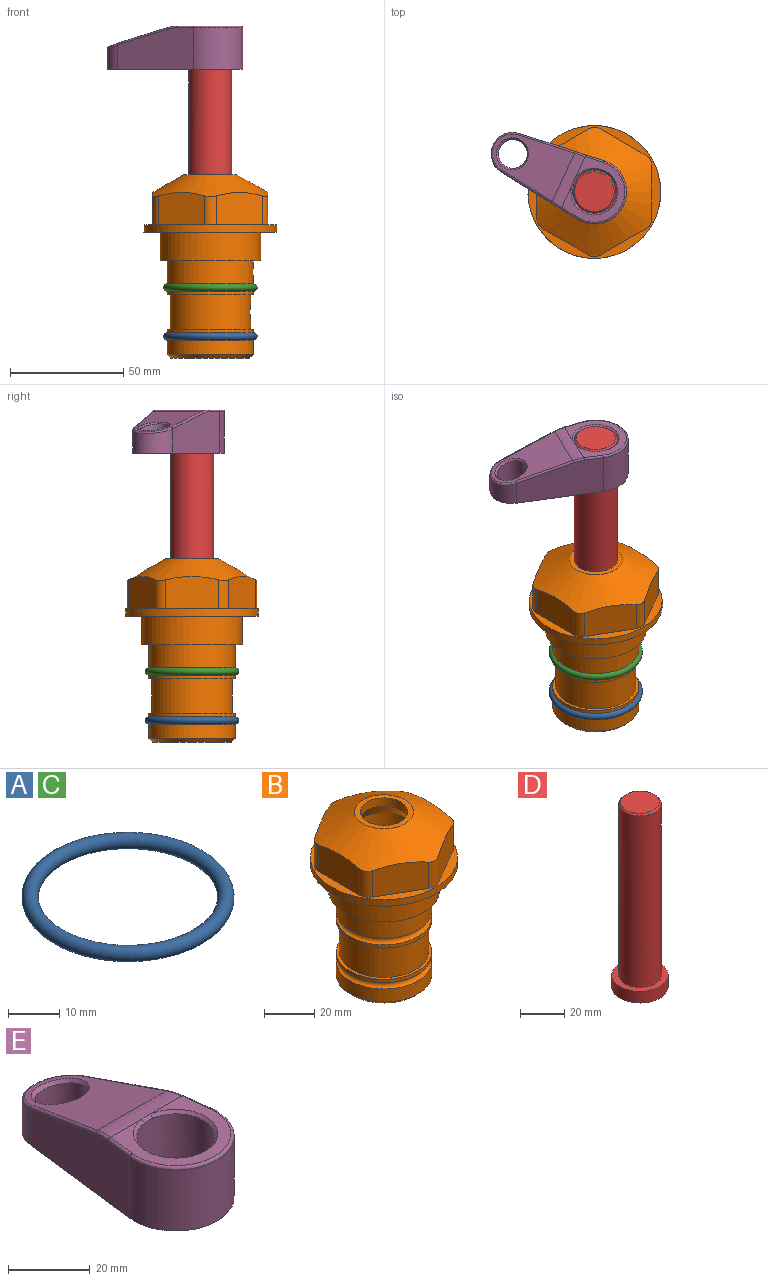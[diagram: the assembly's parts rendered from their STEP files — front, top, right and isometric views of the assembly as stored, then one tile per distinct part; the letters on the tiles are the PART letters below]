
ASSEMBLY  parts=5 mates=4
PART A: 1 faces, bbox 44.7x44.7x3.2 mm
  f0: torus R=19.05mm, axis (0,0,1), area 1193.9mm2
PART B: 36 faces, bbox 58.7x58.7x81 mm
  f0: cylinder r=17.78mm len=35.56mm, axis (0,0,1), area 1670.8mm2, adj f23,f24,f31
  f1: cylinder r=19.05mm len=38.1mm, axis (0,0,1), area 1191.9mm2, adj f26,f27,f30
  f2: plane 58.66x58.66mm, normal (0,0,-1), area 1150.6mm2, adj f3,f28
  f3: cylinder r=29.33mm len=58.66mm, axis (0,0,-1), area 585.1mm2, adj f2,f4
  f4: plane 58.66x58.66mm, normal (0,0,1), area 475.9mm2, adj f3,f5,f6,f7,f8,f9,f10,f11
  f5: plane 20.32x14.34mm, normal (-0.5,0.87,0), area 324.4mm2, adj f4,f15,f16,f17
  f6: plane 20.32x14.34mm, normal (0.5,0.87,0), area 324.4mm2, adj f4,f14,f15,f17
  f7: plane 23.48x14.34mm, normal (1,0,0), area 324.4mm2, adj f4,f13,f14,f17
  f8: plane 20.32x14.34mm, normal (0.5,-0.87,0), area 324.4mm2, adj f4,f12,f13,f17
  f9: plane 20.32x14.34mm, normal (-0.5,-0.87,0), area 324.4mm2, adj f4,f11,f12,f17
  f10: plane 23.48x14.34mm, normal (-1,0,0), area 324.4mm2, adj f4,f11,f16,f17
  f11: cylinder r=5.08mm len=12.85mm, axis (0,0,-1), area 67.2mm2, adj f4,f9,f10,f17
  f12: cylinder r=5.08mm len=12.85mm, axis (0,0,-1), area 67.2mm2, adj f4,f8,f9,f17
  f13: cylinder r=5.08mm len=12.85mm, axis (0,0,-1), area 67.2mm2, adj f4,f7,f8,f17
  f14: cylinder r=5.08mm len=12.85mm, axis (0,0,-1), area 67.2mm2, adj f4,f6,f7,f17
  f15: cylinder r=5.08mm len=12.85mm, axis (0,0,-1), area 67.2mm2, adj f4,f5,f6,f17
  f16: cylinder r=5.08mm len=12.85mm, axis (0,0,-1), area 67.2mm2, adj f4,f5,f10,f17
  f17: cone r=11.73mm half-angle=60deg, axis (0,0,-1), area 2071.8mm2, adj f5,f6,f7,f8,f9,f10,f11,f12
  f18: plane 23.46x23.46mm, normal (0,0,1), area 147.4mm2, adj f17,f35
  f19: plane 34.93x34.93mm, normal (0,0,-1), area 958mm2, adj f29
  f20: cylinder r=19.05mm len=38.1mm, axis (0,0,1), area 760.1mm2, adj f21,f29
  f21: torus R=19.05mm, axis (0,0,1), area 565.3mm2, adj f20,f22
  f22: cylinder r=19.05mm len=38.1mm, axis (0,0,1), area 190mm2, adj f21,f23
  f23: plane 38.1x38.1mm, normal (0,0,1), area 146.9mm2, adj f0,f22
  f24: plane 38.1x38.1mm, normal (0,0,-1), area 146.9mm2, adj f0,f25
  f25: cylinder r=19.05mm len=38.1mm, axis (0,0,1), area 190mm2, adj f24,f26
  f26: torus R=19.05mm, axis (0,0,1), area 565.3mm2, adj f1,f25
  f27: plane 44.45x44.45mm, normal (0,0,-1), area 411.7mm2, adj f1,f28
  f28: cylinder r=22.23mm len=44.45mm, axis (0,0,1), area 1773.5mm2, adj f2,f27
  f29: cone r=19.05mm half-angle=45deg, axis (0,0,1), area 257.5mm2, adj f19,f20
  f30: cylinder r=3.17mm len=6.75mm, axis (-1,0,0), area 128mm2, adj f1,f33
  f31: cylinder r=3.17mm len=6.35mm, axis (-1,0,0), area 102.5mm2, adj f0,f33
  f32: plane 25.4x25.4mm, normal (0,0,1), area 506.7mm2, adj f33
  f33: cylinder r=12.7mm len=66.42mm, axis (0,0,-1), area 5236.2mm2, adj f30,f31,f32,f34
  f34: cone r=9.53mm half-angle=30deg, axis (0,0,-1), area 443.4mm2, adj f33,f35
  f35: cylinder r=9.53mm len=19.05mm, axis (0,0,-1), area 240.9mm2, adj f18,f34
PART C: same geometry as A
PART D: 6 faces, bbox 25.4x25.4x101.6 mm
  f0: plane 17.46x17.46mm, normal (0,0,1), area 239.5mm2, adj f5
  f1: plane 25.4x25.4mm, normal (0,0,-1), area 506.7mm2, adj f2
  f2: cylinder r=12.7mm len=25.4mm, axis (0,0,1), area 506.7mm2, adj f1,f3
  f3: plane 25.4x25.4mm, normal (0,0,1), area 221.7mm2, adj f2,f4
  f4: cylinder r=9.53mm len=94.46mm, axis (0,0,1), area 5653mm2, adj f3,f5
  f5: cone r=8.73mm half-angle=45deg, axis (0,0,-1), area 64.4mm2, adj f0,f4
PART E: 31 faces, bbox 31.7x65.5x19.8 mm
  f0: plane 39.12x18.26mm, normal (0.99,0.12,0), area 612.2mm2, adj f1,f4,f7,f11,f13,f15
  f1: cylinder r=9.53mm len=18.91mm, axis (0,0,-1), area 296.1mm2, adj f0,f2,f7,f17
  f2: plane 39.12x18.26mm, normal (-0.99,0.12,0), area 612.2mm2, adj f1,f4,f7,f12,f14,f16
  f3: cylinder r=6.35mm len=12.7mm, axis (0,0,-1), area 362.4mm2, adj f7,f18
  f4: cylinder r=14.29mm len=28.58mm, axis (0,0,-1), area 882.2mm2, adj f0,f2,f7,f10
  f5: cylinder r=9.53mm len=19.05mm, axis (0,0,-1), area 1092.6mm2, adj f7,f19,f20
  f6: plane 26.99x23.69mm, normal (0,0,1), area 216.2mm2, adj f9,f10,f11,f12,f19
  f7: plane 63.5x28.58mm, normal (0,0,-1), area 661.8mm2, adj f0,f1,f2,f3,f4,f5,f22,f23
  f8: plane 33.52x23.6mm, normal (0,0.26,0.97), area 486mm2, adj f9,f15,f16,f17,f18
  f9: cylinder r=19.05mm len=24.72mm, axis (1,0,0), area 120.4mm2, adj f6,f8,f13,f14,f20
  f10: torus R=13.49mm, axis (0,0,1), area 59mm2, adj f4,f6,f11,f12
  f11: cylinder r=0.79mm len=8.67mm, axis (0.12,-0.99,0), area 10.8mm2, adj f0,f6,f10,f13
  f12: cylinder r=0.79mm len=8.67mm, axis (0.12,0.99,0), area 10.8mm2, adj f2,f6,f10,f14
  f13: bspline ~4.95x1.42mm, area 6.1mm2, adj f0,f9,f11,f15
  f14: bspline ~4.95x1.42mm, area 6.1mm2, adj f2,f9,f12,f16
  f15: cylinder r=0.79mm len=25.95mm, axis (0.12,-0.96,0.26), area 32.9mm2, adj f0,f8,f13,f17
  f16: cylinder r=0.79mm len=25.95mm, axis (0.12,0.96,-0.26), area 32.9mm2, adj f2,f8,f14,f17
  f17: bspline ~18.91x8.38mm, area 30mm2, adj f1,f8,f15,f16
  f18: bspline ~14.29x14.29mm, area 48.3mm2, adj f3,f8
  f19: cone r=9.53mm half-angle=45deg, axis (0,0,1), area 66.5mm2, adj f5,f6,f20
  f20: bspline ~3.22x0.96mm, area 3.5mm2, adj f5,f9,f19
  f21: plane 2.75x2.72mm, normal (0,0,-1), area 2.9mm2, adj f23,f25,f28
  f22: plane 23.05x15.88mm, normal (-0.99,-0.12,0), area 323.6mm2, adj f7,f25,f26,f27,f28,f29
  f23: plane 23.05x15.88mm, normal (0.99,-0.12,0), area 323.6mm2, adj f7,f21,f25,f27,f28,f30
  f24: cylinder r=9.53mm len=10.69mm, axis (0,0,-1), area 114.7mm2, adj f7,f27,f29,f30
  f25: cylinder r=12.7mm len=20.59mm, axis (0,0,-1), area 381.1mm2, adj f7,f21,f22,f23,f26,f28
  f26: plane 2.75x2.72mm, normal (0,0,-1), area 2.9mm2, adj f22,f25,f28
  f27: plane 19.72x18.37mm, normal (0,-0.26,-0.97), area 291.8mm2, adj f22,f23,f24,f28,f29,f30
  f28: cylinder r=15.88mm len=19.92mm, axis (1,0,0), area 54.8mm2, adj f21,f22,f23,f25,f26,f27
  f29: cylinder r=1.59mm len=11mm, axis (0,0,-1), area 34.7mm2, adj f7,f22,f24,f27
  f30: cylinder r=1.59mm len=11mm, axis (0,0,-1), area 34.7mm2, adj f7,f23,f24,f27
PLACE A t=(0,0,-21.59)mm
PLACE B at identity fixed
PLACE C at identity
PLACE D rot(axis=(0,0,1),65.2deg) t=(0,0,27.55)mm
PLACE E rot(axis=(0,0,1),65.2deg) t=(0,0,27.55)mm
MATE cylindrical B.f0 <-> D.f2  axis (0,0,1) through (0,0,-50.55)mm
MATE fastened C.f0 <-> B.f0  axis (0,0,1) through (0,0,-24.51)mm
MATE fastened A.f0 <-> B.f0  axis (0,0,1) through (0,0,-46.1)mm
MATE fastened E.f4 <-> D.f2  axis (0,0,1) through (0,0,91.05)mm
